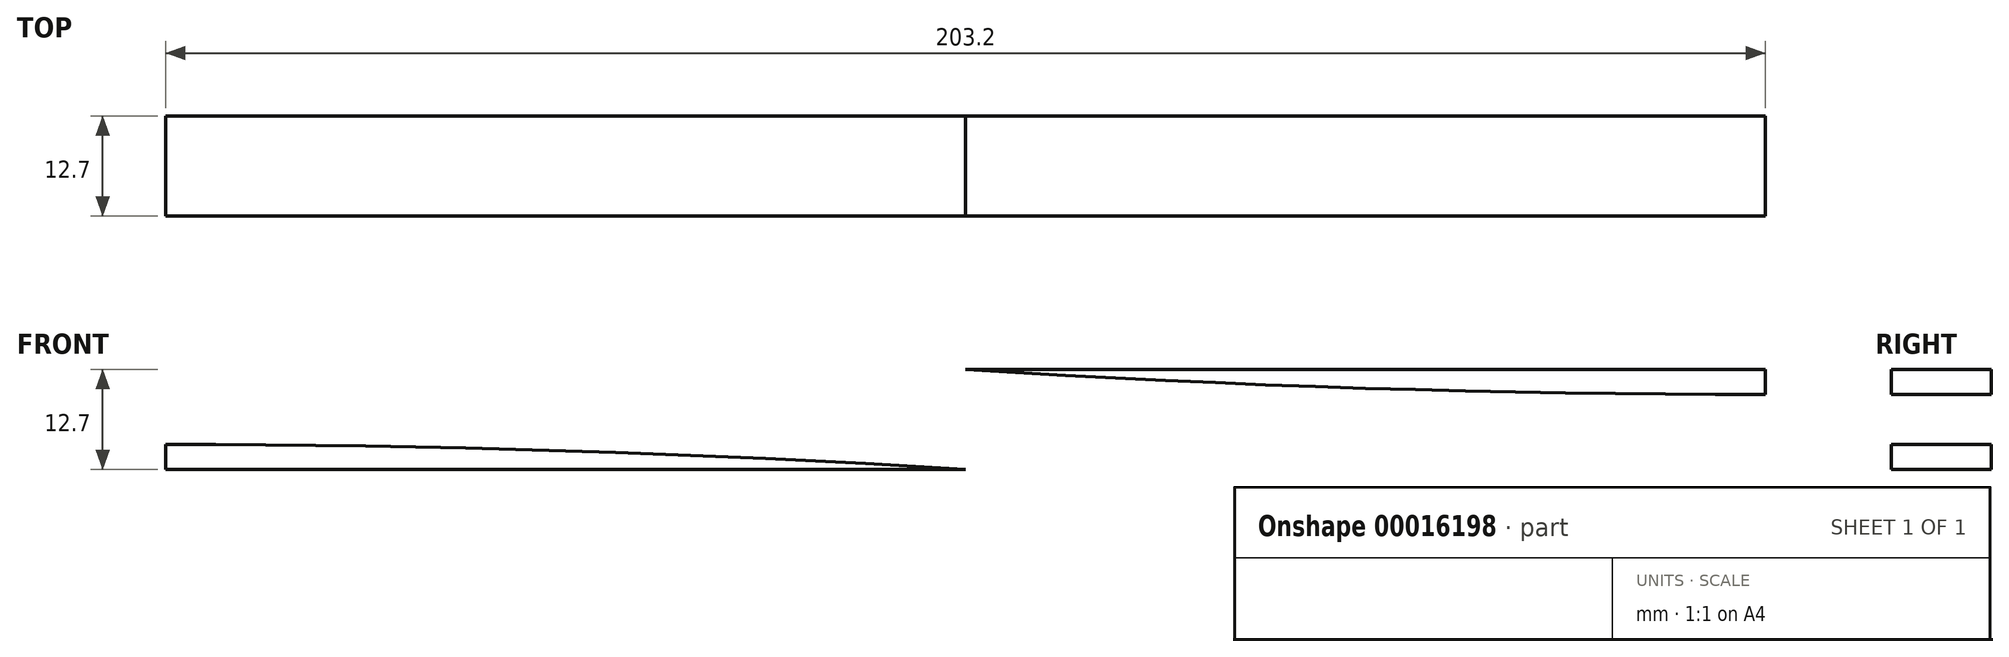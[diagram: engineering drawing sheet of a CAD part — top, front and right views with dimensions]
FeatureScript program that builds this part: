
annotation { "Feature Type Name" : "Feature", "Feature Type Description" : "" }
export const myFeature = defineFeature(function(context is Context, id is Id, definition is map)
    precondition{}
    {
        {
            var Q0;
            Q0=qCreatedBy(makeId("Top.planeOp"),FACE);
            var sketch = newSketch(context, id + "F0", { "sketchPlane" : qUnion([Q0])});
            skLineSegment(sketch, "E0.rect.bottom", {"start": v(-101.6, 6.35) * mm, "end": v(101.6, 6.35) * mm});
            skLineSegment(sketch, "E0.rect.top", {"start": v(-101.6, -6.35) * mm, "end": v(101.6, -6.35) * mm});
            skLineSegment(sketch, "E0.rect.left", {"start": v(-101.6, 6.35) * mm, "end": v(-101.6, -6.35) * mm});
            skLineSegment(sketch, "E0.rect.right", {"start": v(101.6, 6.35) * mm, "end": v(101.6, -6.35) * mm});
            skPoint(sketch, "E0.rect.middle", {"position": v(0, 0) * mm});
            skSolve(sketch);
        }
        {
            var Q0;
            Q0=makeQuery(id+"F0.imprint","IMPRINT",FACE,{"disambiguationData":[TD([[makeQuery(id+"F0.imprint","IMPRINT",EDGE,{"derivedFrom":sQuery(id+"F0.wireOp",EDGE,"E0.rect.bottom")}),-1.0]])]});
            extrude(context, id + "F1", {"entities" : qUnion([Q0]), "endBound" : BoundingType.SYMMETRIC, "depth" : 12.7 * mm});
        }
        {
            var Q0;
            Q0=makeQuery(id+"F1.opExtrude","SWEPT_FACE",FACE,{"disambiguationData":[OSD([sQuery(id+"F0.wireOp",EDGE,"E0.rect.top")])]});
            var sketch = newSketch(context, id + "F2", { "sketchPlane" : qUnion([Q0])});
            skLineSegment(sketch, "E1", {"start": v(-101.6, 0) * mm, "end": v(101.6, 0) * mm, "construction": true});
            skLineSegment(sketch, "E2", {"start": v(0, 6.35) * mm, "end": v(0, -6.35) * mm, "construction": true});
            skLineSegment(sketch, "E3", {"start": v(-101.6, 3.18) * mm, "end": v(0, 3.18) * mm, "construction": true});
            skArc(sketch, "E4", {"start": v(-101.6, 3.18) * mm, "mid": v(-50.78, 3.97) * mm, "end": v(0, 6.35) * mm});
            skArc(sketch, "E5.MirrorCS", {"start": v(-101.6, -3.18) * mm, "mid": v(-50.78, -3.97) * mm, "end": v(0, -6.35) * mm});
            skArc(sketch, "E6.MirrorCS", {"start": v(101.6, -3.18) * mm, "mid": v(50.78, -3.97) * mm, "end": v(0, -6.35) * mm});
            skArc(sketch, "E7.MirrorCS", {"start": v(101.6, 3.18) * mm, "mid": v(50.78, 3.97) * mm, "end": v(0, 6.35) * mm});
            skLineSegment(sketch, "E8.rect.bottom", {"start": v(-6.35, 1.59) * mm, "end": v(6.35, 1.59) * mm});
            skLineSegment(sketch, "E8.rect.top", {"start": v(-6.35, -1.59) * mm, "end": v(6.35, -1.59) * mm});
            skLineSegment(sketch, "E8.rect.left", {"start": v(-6.35, 1.59) * mm, "end": v(-6.35, -1.59) * mm});
            skLineSegment(sketch, "E8.rect.right", {"start": v(6.35, 1.59) * mm, "end": v(6.35, -1.59) * mm});
            skPoint(sketch, "E8.rect.middle", {"position": v(0, 0) * mm});
            skSolve(sketch);
        }
        {
            var Q0;
            Q0 = qSketchRegion(id + "F2", true);
            extrude(context, id + "F3", {"entities" : qUnion([Q0]), "operationType" : NewBodyOperationType.REMOVE, "oppositeDirection" : true, "depth" : 25.4 * mm});
        }
        {
            var Q0;
            {var subQ2=sQuery(id+"F2.wireOp",EDGE,"E4");Q0=makeQuery(id+"F2.imprint","IMPRINT",FACE,{"disambiguationData":[TD([[makeQuery(id+"F2.imprint","IMPRINT",EDGE,{"derivedFrom":subQ2}),1.0]])]});}
            var Q1;
            {var subQ2=sQuery(id+"F2.wireOp",EDGE,"E5.MirrorCS");Q1=makeQuery(id+"F2.imprint","IMPRINT",FACE,{"disambiguationData":[TD([[makeQuery(id+"F2.imprint","IMPRINT",EDGE,{"derivedFrom":subQ2}),-1.0]])]});}
            var Q2;
            {var subQ2=sQuery(id+"F2.wireOp",EDGE,"E7.MirrorCS");Q2=makeQuery(id+"F2.imprint","IMPRINT",FACE,{"disambiguationData":[TD([[makeQuery(id+"F2.imprint","IMPRINT",EDGE,{"derivedFrom":subQ2}),-1.0]])]});}
            var Q3;
            {var subQ2=sQuery(id+"F2.wireOp",EDGE,"E6.MirrorCS");Q3=makeQuery(id+"F2.imprint","IMPRINT",FACE,{"disambiguationData":[TD([[makeQuery(id+"F2.imprint","IMPRINT",EDGE,{"derivedFrom":subQ2}),1.0]])]});}
            extrude(context, id + "F4", {"entities" : qUnion([Q0, Q1, Q2, Q3]), "operationType" : NewBodyOperationType.REMOVE, "oppositeDirection" : true, "depth" : 25.4 * mm});
        }
        {
            var Q0;
            Q0=makeQuery(id+"F2.imprint","IMPRINT",FACE,{"disambiguationData":[TD([[makeQuery(id+"F2.imprint","IMPRINT",EDGE,{"derivedFrom":sQuery(id+"F2.wireOp",EDGE,"E8.rect.bottom")}),-1.0]])]});
            extrude(context, id + "F5", {"entities" : qUnion([Q0]), "operationType" : NewBodyOperationType.REMOVE, "oppositeDirection" : true, "depth" : 25.4 * mm});
        }
    });
